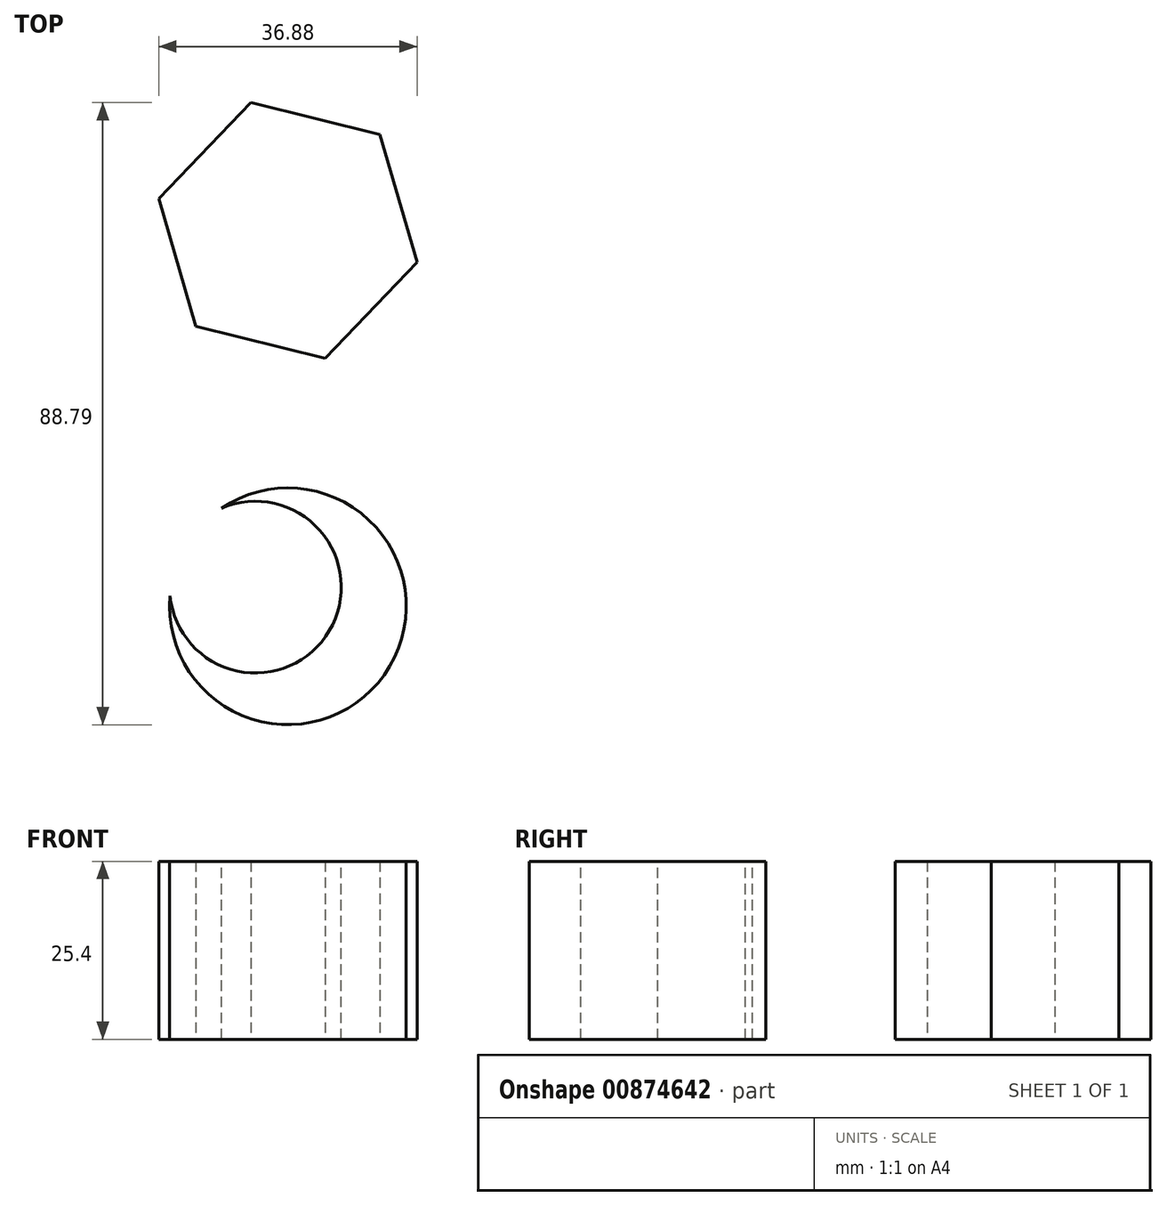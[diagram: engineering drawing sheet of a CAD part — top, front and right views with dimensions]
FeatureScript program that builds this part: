
annotation { "Feature Type Name" : "Feature", "Feature Type Description" : "" }
export const myFeature = defineFeature(function(context is Context, id is Id, definition is map)
    precondition{}
    {
        {
            var Q0;
            Q0=qCreatedBy(makeId("Top.planeOp"),FACE);
            var sketch = newSketch(context, id + "F0", { "sketchPlane" : qUnion([Q0])});
            skCircle(sketch, "E0", {"center": v(0, 0) * mm, "radius": 16.9 * mm});
            skCircle(sketch, "E1.cCircle", {"center": v(0, 53.65) * mm, "radius": 16.45 * mm, "construction": true});
            skLineSegment(sketch, "E1.0", {"start": v(13.14, 67.36) * mm, "end": v(18.44, 49.13) * mm});
            skLineSegment(sketch, "E1.1", {"start": v(18.44, 49.13) * mm, "end": v(5.3, 35.42) * mm});
            skLineSegment(sketch, "E1.2", {"start": v(5.3, 35.42) * mm, "end": v(-13.14, 39.94) * mm});
            skLineSegment(sketch, "E1.3", {"start": v(-13.14, 39.94) * mm, "end": v(-18.44, 58.17) * mm});
            skLineSegment(sketch, "E1.4", {"start": v(-18.44, 58.17) * mm, "end": v(-5.3, 71.89) * mm});
            skLineSegment(sketch, "E1.5", {"start": v(-5.3, 71.89) * mm, "end": v(13.14, 67.36) * mm});
            skPoint(sketch, "E1.0.midPoint", {"position": v(15.8, 58.25) * mm});
            skSolve(sketch);
        }
        {
            var Q0;
            Q0 = qSketchRegion(id + "F0", true);
            extrude(context, id + "F1", {"entities" : qUnion([Q0]), "depth" : 25.4 * mm, "offsetDistance" : 25.4 * mm});
        }
        {
            var Q0;
            Q0=makeQuery(id+"F1.opExtrude","CAP_FACE",FACE,{"disambiguationData":[OSD([sQuery(id+"F0.wireOp",EDGE,"E0")])],"isStart":false});
            var sketch = newSketch(context, id + "F2", { "sketchPlane" : qUnion([Q0])});
            skCircle(sketch, "E2", {"center": v(-4.64, 2.73) * mm, "radius": 12.26 * mm});
            skSolve(sketch);
        }
        {
            var Q0;
            {var subQ0=sQuery(id+"F2.wireOp",EDGE,"E2");var subQ1=makeQuery(id+"F1.opExtrude","CAP_EDGE",EDGE,{"disambiguationData":[OSD([sQuery(id+"F0.wireOp",EDGE,"E0")])],"isStart":false});var subQ2=makeQuery(id+"F2.imprint","INTERSECT",VERTEX,{"disambiguationData":[OD(0.0)],"derivedFrom":[subQ1,subQ0]});Q0=makeQuery(id+"F2.imprint","IMPRINT",FACE,{"disambiguationData":[TD([[makeQuery(id+"F2.imprint","IMPRINT",EDGE,{"disambiguationData":[TD([[subQ2,-1.0]])],"derivedFrom":subQ0}),1.0]])]});}
            extrude(context, id + "F3", {"entities" : qUnion([Q0]), "operationType" : NewBodyOperationType.REMOVE, "oppositeDirection" : true, "depth" : 25.4 * mm, "offsetDistance" : 25.4 * mm});
        }
    });
